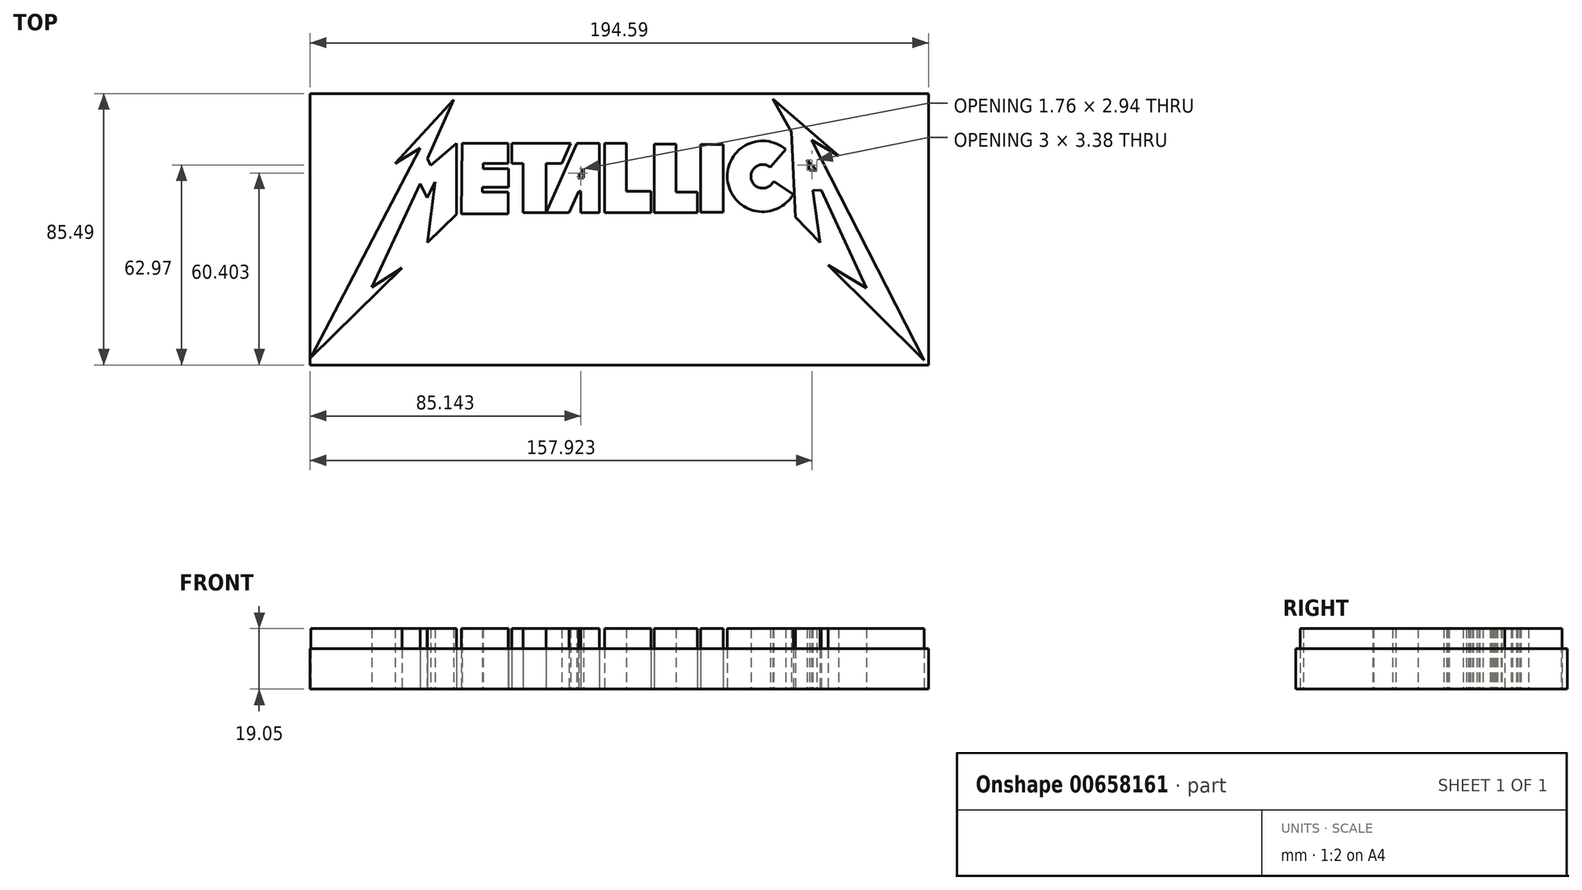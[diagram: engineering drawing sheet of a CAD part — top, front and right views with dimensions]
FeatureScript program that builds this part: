
annotation { "Feature Type Name" : "Feature", "Feature Type Description" : "" }
export const myFeature = defineFeature(function(context is Context, id is Id, definition is map)
    precondition{}
    {
        {
            var Q0;
            Q0=qCreatedBy(makeId("Top.planeOp"),FACE);
            var sketch = newSketch(context, id + "F0", { "sketchPlane" : qUnion([Q0])});
            skLineSegment(sketch, "E0", {"start": v(-94.85, -30.84) * mm, "end": v(-60.46, 35) * mm});
            skLineSegment(sketch, "E1", {"start": v(-60.46, 35) * mm, "end": v(-68.34, 30.23) * mm});
            skLineSegment(sketch, "E2", {"start": v(-68.34, 30.23) * mm, "end": v(-49.85, 50.32) * mm});
            skLineSegment(sketch, "E3", {"start": v(-49.85, 50.32) * mm, "end": v(-58.14, 31.72) * mm});
            skLineSegment(sketch, "E4", {"start": v(-58.14, 31.72) * mm, "end": v(-57.16, 29.56) * mm});
            skLineSegment(sketch, "E5", {"start": v(-57.16, 29.56) * mm, "end": v(-49.01, 36.6) * mm});
            skLineSegment(sketch, "E6", {"start": v(-49.01, 36.6) * mm, "end": v(-49.01, 14.25) * mm});
            skLineSegment(sketch, "E7", {"start": v(-49.01, 14.25) * mm, "end": v(-58.18, 5.3) * mm});
            skLineSegment(sketch, "E8", {"start": v(-58.18, 5.3) * mm, "end": v(-55.72, 24.4) * mm});
            skLineSegment(sketch, "E9", {"start": v(-55.72, 24.4) * mm, "end": v(-58.31, 19.43) * mm});
            skLineSegment(sketch, "E10", {"start": v(-58.31, 19.43) * mm, "end": v(-60.46, 23.81) * mm});
            skLineSegment(sketch, "E11", {"start": v(-60.46, 23.81) * mm, "end": v(-75.66, -8.77) * mm});
            skLineSegment(sketch, "E12", {"start": v(-75.66, -8.77) * mm, "end": v(-66.19, -2.7) * mm});
            skLineSegment(sketch, "E13", {"start": v(-66.19, -2.7) * mm, "end": v(-94.85, -30.84) * mm});
            skLineSegment(sketch, "E14", {"start": v(-47.23, 36.6) * mm, "end": v(-32.74, 36.6) * mm});
            skLineSegment(sketch, "E15", {"start": v(-32.74, 36.6) * mm, "end": v(-32.74, 30.23) * mm});
            skLineSegment(sketch, "E16", {"start": v(-32.74, 30.23) * mm, "end": v(-40.68, 30.23) * mm});
            skLineSegment(sketch, "E17", {"start": v(-40.68, 30.23) * mm, "end": v(-40.68, 28.53) * mm});
            skLineSegment(sketch, "E18", {"start": v(-40.68, 28.53) * mm, "end": v(-32.67, 28.53) * mm});
            skLineSegment(sketch, "E19", {"start": v(-32.67, 28.53) * mm, "end": v(-32.67, 22.68) * mm});
            skLineSegment(sketch, "E20", {"start": v(-32.67, 22.68) * mm, "end": v(-40.82, 22.68) * mm});
            skLineSegment(sketch, "E21", {"start": v(-40.82, 22.68) * mm, "end": v(-40.82, 21.22) * mm});
            skLineSegment(sketch, "E22", {"start": v(-40.82, 21.22) * mm, "end": v(-32.74, 21.22) * mm});
            skLineSegment(sketch, "E23", {"start": v(-32.74, 21.22) * mm, "end": v(-32.74, 14.4) * mm});
            skLineSegment(sketch, "E24", {"start": v(-32.74, 14.4) * mm, "end": v(-47.43, 14.4) * mm});
            skLineSegment(sketch, "E25", {"start": v(-47.43, 14.4) * mm, "end": v(-47.23, 36.6) * mm});
            skLineSegment(sketch, "E26", {"start": v(-31.66, 36.6) * mm, "end": v(-13, 36.6) * mm});
            skLineSegment(sketch, "E27", {"start": v(-13, 36.6) * mm, "end": v(-15.87, 30.23) * mm});
            skLineSegment(sketch, "E28", {"start": v(-15.87, 30.23) * mm, "end": v(-20.85, 30.23) * mm});
            skLineSegment(sketch, "E29", {"start": v(-20.85, 30.23) * mm, "end": v(-20.85, 14.68) * mm});
            skLineSegment(sketch, "E30", {"start": v(-20.85, 14.68) * mm, "end": v(-28.1, 14.68) * mm});
            skLineSegment(sketch, "E31", {"start": v(-28.1, 14.68) * mm, "end": v(-28.1, 30.23) * mm});
            skLineSegment(sketch, "E32", {"start": v(-28.1, 30.23) * mm, "end": v(-31.66, 30.23) * mm});
            skLineSegment(sketch, "E33", {"start": v(-31.66, 30.23) * mm, "end": v(-31.66, 36.6) * mm});
            skPoint(sketch, "E34.orphan", {"position": v(-31.92, 36.6) * mm});
            skLineSegment(sketch, "E35", {"start": v(-11.18, 36.4) * mm, "end": v(-20.85, 14.68) * mm});
            skLineSegment(sketch, "E36", {"start": v(-13.6, 14.68) * mm, "end": v(-10.54, 21.46) * mm});
            skLineSegment(sketch, "E37", {"start": v(-10.54, 21.46) * mm, "end": v(-9.85, 21.46) * mm});
            skLineSegment(sketch, "E38", {"start": v(-9.85, 21.46) * mm, "end": v(-9.85, 14.68) * mm});
            skLineSegment(sketch, "E39", {"start": v(-9.85, 14.68) * mm, "end": v(-4.01, 14.68) * mm});
            skLineSegment(sketch, "E40", {"start": v(-4.01, 14.68) * mm, "end": v(-4.01, 36.57) * mm});
            skLineSegment(sketch, "E41", {"start": v(-4.01, 36.57) * mm, "end": v(-11.11, 36.57) * mm});
            skLineSegment(sketch, "E42", {"start": v(-11.18, 36.4) * mm, "end": v(-11.11, 36.57) * mm});
            skLineSegment(sketch, "E43", {"start": v(-10.79, 25.68) * mm, "end": v(-9.03, 25.68) * mm});
            skLineSegment(sketch, "E44", {"start": v(-9.03, 25.68) * mm, "end": v(-9.03, 28.62) * mm});
            skLineSegment(sketch, "E45", {"start": v(-9.03, 28.62) * mm, "end": v(-10.79, 25.68) * mm});
            skLineSegment(sketch, "E46", {"start": v(-2.35, 36.53) * mm, "end": v(4.5, 36.53) * mm});
            skLineSegment(sketch, "E47", {"start": v(4.5, 36.53) * mm, "end": v(4.5, 21.4) * mm});
            skLineSegment(sketch, "E48", {"start": v(4.5, 21.4) * mm, "end": v(12.23, 21.4) * mm});
            skLineSegment(sketch, "E49", {"start": v(12.23, 21.4) * mm, "end": v(12.23, 14.7) * mm});
            skLineSegment(sketch, "E50", {"start": v(12.23, 14.7) * mm, "end": v(-2.33, 14.7) * mm});
            skLineSegment(sketch, "E51", {"start": v(-2.33, 14.7) * mm, "end": v(-2.35, 36.53) * mm});
            skLineSegment(sketch, "E52", {"start": v(13.23, 36.33) * mm, "end": v(13.23, 14.7) * mm});
            skLineSegment(sketch, "E53", {"start": v(13.23, 14.7) * mm, "end": v(26.76, 14.7) * mm});
            skLineSegment(sketch, "E54", {"start": v(26.76, 14.7) * mm, "end": v(26.76, 21.15) * mm});
            skLineSegment(sketch, "E55", {"start": v(26.76, 21.15) * mm, "end": v(20.05, 21.15) * mm});
            skLineSegment(sketch, "E56", {"start": v(20.05, 21.15) * mm, "end": v(20.05, 36.33) * mm});
            skLineSegment(sketch, "E57", {"start": v(20.05, 36.33) * mm, "end": v(13.23, 36.33) * mm});
            skPoint(sketch, "E58.orphan", {"position": v(13.23, 36.53) * mm});
            skLineSegment(sketch, "E59", {"start": v(27.92, 36.2) * mm, "end": v(34.97, 36.2) * mm});
            skLineSegment(sketch, "E60", {"start": v(34.97, 36.2) * mm, "end": v(34.97, 14.81) * mm});
            skLineSegment(sketch, "E61", {"start": v(27.79, 14.81) * mm, "end": v(34.97, 14.81) * mm});
            skLineSegment(sketch, "E62", {"start": v(27.79, 14.81) * mm, "end": v(27.79, 36.2) * mm});
            skLineSegment(sketch, "E63", {"start": v(27.79, 36.2) * mm, "end": v(27.92, 36.2) * mm});
            skArc(sketch, "E64", {"start": v(54.63, 34.64) * mm, "mid": v(36.38, 24.32) * mm, "end": v(57, 20.5) * mm});
            skLineSegment(sketch, "E65", {"start": v(54.63, 34.64) * mm, "end": v(49.78, 29.02) * mm});
            skLineSegment(sketch, "E66", {"start": v(50.8, 24.64) * mm, "end": v(57, 20.5) * mm});
            skArc(sketch, "E67", {"start": v(49.78, 29.02) * mm, "mid": v(43.74, 25.31) * mm, "end": v(50.8, 24.64) * mm});
            skLineSegment(sketch, "E68", {"start": v(50.6, 50.54) * mm, "end": v(56.46, 40.08) * mm});
            skLineSegment(sketch, "E69", {"start": v(56.46, 40.08) * mm, "end": v(57.67, 13.38) * mm});
            skLineSegment(sketch, "E70", {"start": v(57.67, 13.38) * mm, "end": v(65.42, 5.26) * mm});
            skLineSegment(sketch, "E71", {"start": v(65.42, 5.26) * mm, "end": v(63.09, 21.66) * mm});
            skLineSegment(sketch, "E72", {"start": v(63.09, 21.66) * mm, "end": v(65.82, 21.78) * mm});
            skLineSegment(sketch, "E73", {"start": v(65.82, 21.78) * mm, "end": v(80.04, -8.97) * mm});
            skLineSegment(sketch, "E74", {"start": v(80.04, -8.97) * mm, "end": v(68.02, -1.8) * mm});
            skLineSegment(sketch, "E75", {"start": v(68.02, -1.8) * mm, "end": v(98.22, -31.78) * mm});
            skLineSegment(sketch, "E76", {"start": v(98.22, -31.78) * mm, "end": v(62.78, 37.63) * mm});
            skLineSegment(sketch, "E77", {"start": v(62.78, 37.63) * mm, "end": v(71.22, 32.6) * mm});
            skLineSegment(sketch, "E78", {"start": v(71.22, 32.6) * mm, "end": v(50.6, 50.54) * mm});
            skLineSegment(sketch, "E79", {"start": v(-20.85, 14.68) * mm, "end": v(-13.6, 14.68) * mm});
            skLineSegment(sketch, "E80", {"start": v(62.1, 28.03) * mm, "end": v(64.38, 28.03) * mm});
            skLineSegment(sketch, "E81", {"start": v(62.1, 28.03) * mm, "end": v(61.37, 31.41) * mm});
            skLineSegment(sketch, "E82", {"start": v(61.37, 31.41) * mm, "end": v(64.38, 28.03) * mm});
            skSolve(sketch);
        }
        {
            var Q0;
            Q0=qCreatedBy(makeId("Top.planeOp"),FACE);
            var sketch = newSketch(context, id + "F1", { "sketchPlane" : qUnion([Q0])});
            skLineSegment(sketch, "E83.bottom", {"start": v(-95.05, 52.24) * mm, "end": v(99.54, 52.24) * mm});
            skLineSegment(sketch, "E83.top", {"start": v(-95.05, -33.25) * mm, "end": v(99.54, -33.25) * mm});
            skLineSegment(sketch, "E83.left", {"start": v(-95.05, 52.24) * mm, "end": v(-95.05, -33.25) * mm});
            skLineSegment(sketch, "E83.right", {"start": v(99.54, 52.24) * mm, "end": v(99.54, -33.25) * mm});
            skSolve(sketch);
        }
        {
            var Q0;
            Q0 = qSketchRegion(id + "F0", true);
            extrude(context, id + "F2", {"entities" : qUnion([Q0]), "depth" : 19.05 * mm, "offsetDistance" : 25.4 * mm});
        }
        {
            var Q0;
            Q0 = qSketchRegion(id + "F1", true);
            extrude(context, id + "F3", {"entities" : qUnion([Q0]), "depth" : 12.7 * mm, "offsetDistance" : 25.4 * mm});
        }
    });
